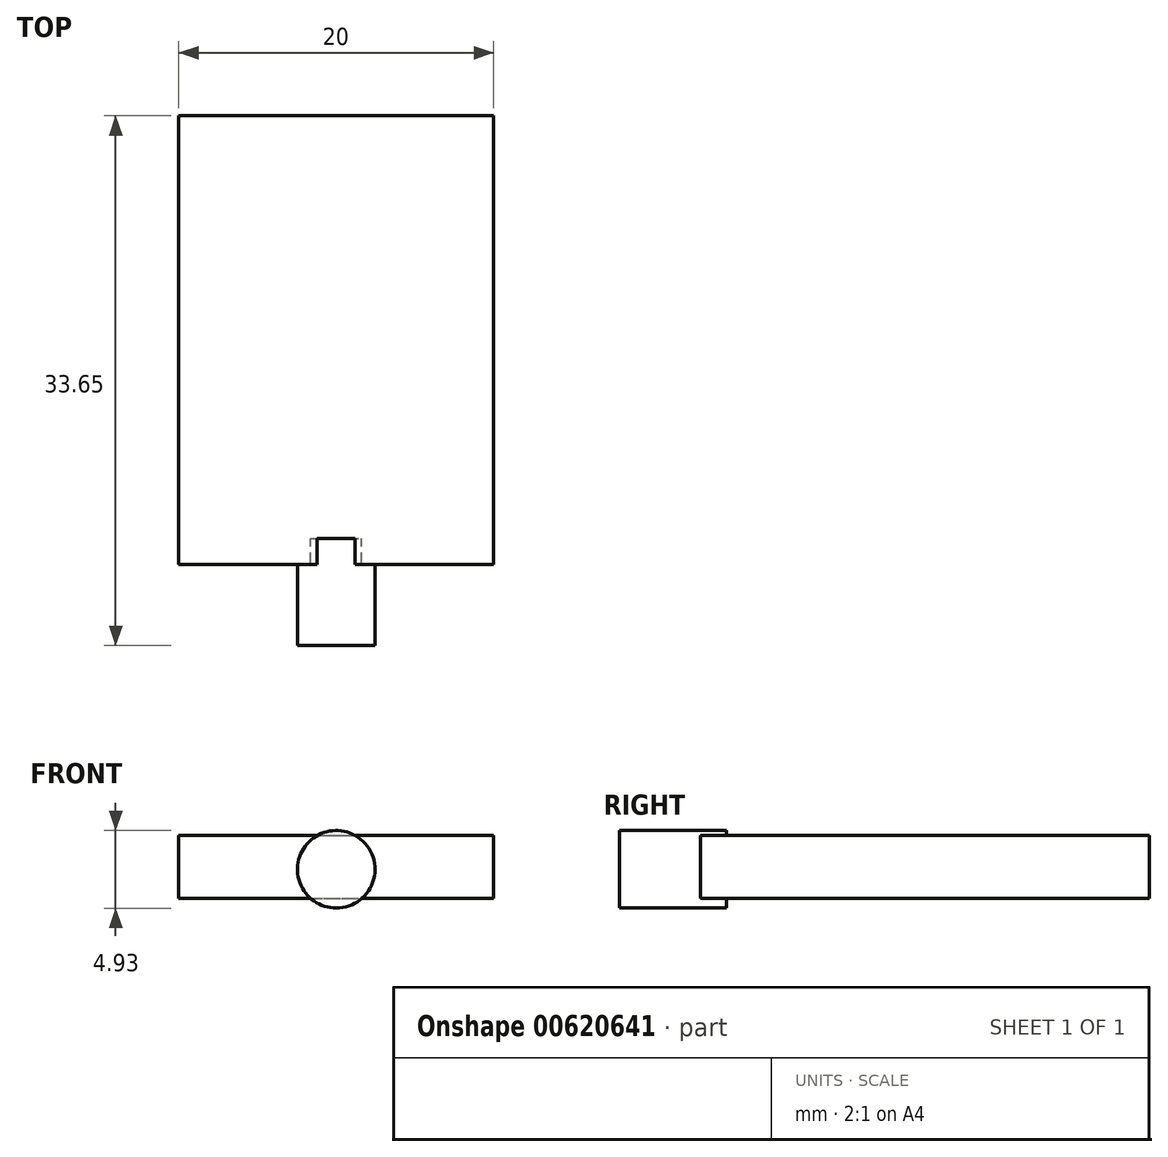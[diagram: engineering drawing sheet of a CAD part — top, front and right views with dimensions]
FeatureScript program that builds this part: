
annotation { "Feature Type Name" : "Feature", "Feature Type Description" : "" }
export const myFeature = defineFeature(function(context is Context, id is Id, definition is map)
    precondition{}
    {
        {
            var Q0;
            Q0=qCreatedBy(makeId("Top.planeOp"),FACE);
            var sketch = newSketch(context, id + "F0", { "sketchPlane" : qUnion([Q0])});
            skLineSegment(sketch, "E0.bottom", {"start": v(-10, 14.25) * mm, "end": v(10, 14.25) * mm});
            skLineSegment(sketch, "E0.top", {"start": v(-10, -14.25) * mm, "end": v(10, -14.25) * mm});
            skLineSegment(sketch, "E0.left", {"start": v(-10, 14.25) * mm, "end": v(-10, -14.25) * mm});
            skLineSegment(sketch, "E0.right", {"start": v(10, 14.25) * mm, "end": v(10, -14.25) * mm});
            skPoint(sketch, "E0.middle", {"position": v(0, 0) * mm});
            skSolve(sketch);
        }
        {
            var Q0;
            Q0=makeQuery(id+"F0.imprint","IMPRINT",FACE,{"disambiguationData":[TD([[makeQuery(id+"F0.imprint","IMPRINT",EDGE,{"derivedFrom":sQuery(id+"F0.wireOp",EDGE,"E0.bottom")}),-1.0]])]});
            extrude(context, id + "F1", {"entities" : qUnion([Q0]), "depth" : 4 * mm, "offsetDistance" : 25 * mm});
        }
        {
            var Q0;
            Q0=qCreatedBy(makeId("Front.planeOp"),FACE);
            var sketch = newSketch(context, id + "F2", { "sketchPlane" : qUnion([Q0])});
            skCircle(sketch, "E1", {"center": v(0, 1.85) * mm, "radius": 2.46 * mm});
            skSolve(sketch);
        }
        {
            var Q0;
            Q0 = qSketchRegion(id + "F2", true);
            extrude(context, id + "F3", {"entities" : qUnion([Q0]), "operationType" : NewBodyOperationType.ADD, "depth" : 19.4 * mm, "offsetDistance" : 25 * mm, "hasSecondDirection" : true, "secondDirectionOppositeDirection" : false, "secondDirectionDepth" : 12.6 * mm});
        }
    });
